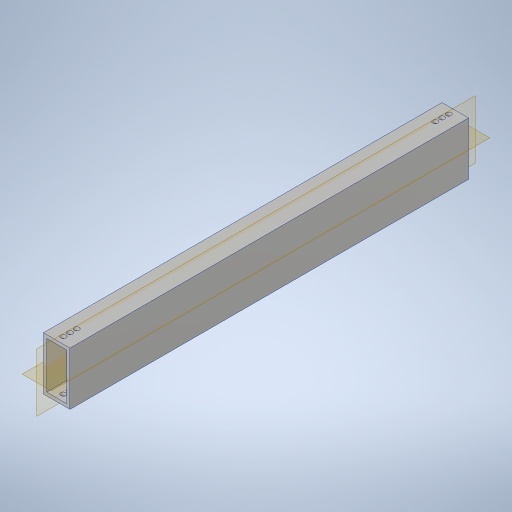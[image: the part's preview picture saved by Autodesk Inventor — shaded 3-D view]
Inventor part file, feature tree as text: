
AUTODESK INVENTOR PART (.ipt)
format: ipt  version: 2023.4 (Build 274418000, 418)  size: 263,680 bytes
history: native  units: in
note: dims shown in document units (in); Inventor stores cm internally (conversion verified against a paired STEP export)
features: extrude x1, hole x1, sketch x1
ambient origin geometry x8: Origin, YZ Plane, XZ Plane, XY Plane, X Axis, Y Axis, Z Axis, Center Point
bodies: Solid1 (feature_tree)
feature tree (3):
  extrude  "Extrusion1"  Depth=1.0in
  hole  "Hole1"  [1 undecoded]
  sketch  "Sketch2"  dims[d4=0.0in d5=0.25in d6=0.25in d7=0.25in d8=0.5in d9=0.201in d10=0.75in d11=0.385in d12=0.25in d13=0.5635in d14=1.0in d15=0.8108in d16=0.5in d17=0.25in d18=0.25in d19=0.25in]
note: 1 required parameter value undecoded (feature->parameter linkage not recoverable at this tier; creation-order binding heuristic only, values carry confidence <= 0.55)
